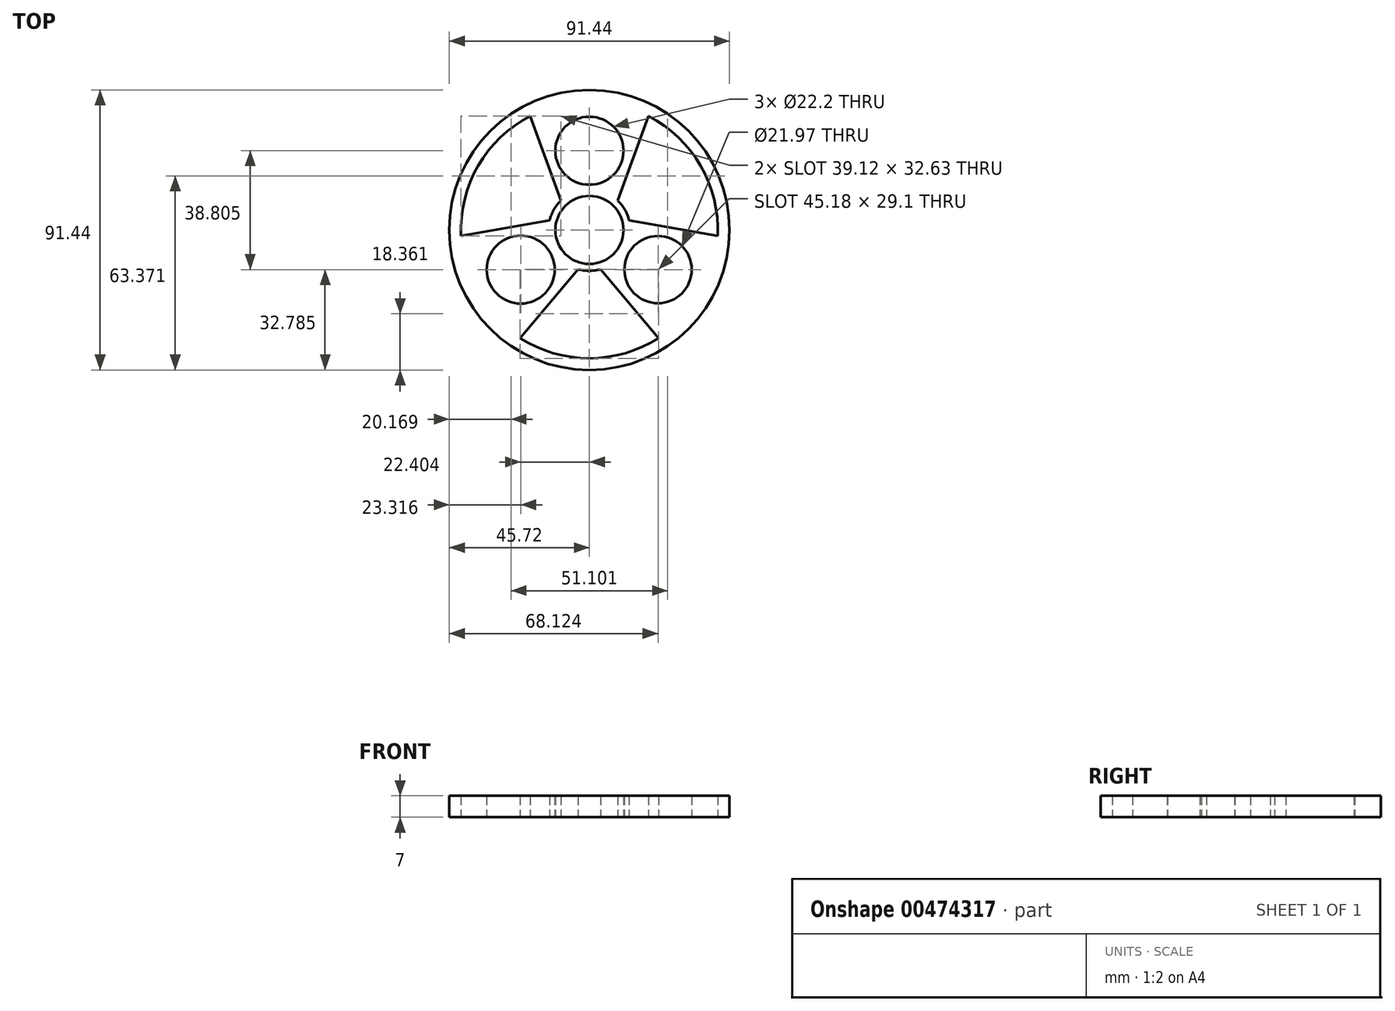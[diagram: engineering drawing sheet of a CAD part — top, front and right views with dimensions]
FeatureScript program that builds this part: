
annotation { "Feature Type Name" : "Feature", "Feature Type Description" : "" }
export const myFeature = defineFeature(function(context is Context, id is Id, definition is map)
    precondition{}
    {
        {
            var Q0;
            Q0=qCreatedBy(makeId("Top.planeOp"),FACE);
            var sketch = newSketch(context, id + "F0", { "sketchPlane" : qUnion([Q0])});
            skCircle(sketch, "E0", {"center": v(0, 0) * mm, "radius": 11.1 * mm});
            skCircle(sketch, "E1", {"center": v(0, 25.87) * mm, "radius": 11.1 * mm});
            skCircle(sketch, "E2.1.1", {"center": v(-22.4, -12.93) * mm, "radius": 11.1 * mm});
            skCircle(sketch, "E2.2.1", {"center": v(22.4, -12.94) * mm, "radius": 10.98 * mm});
            skPoint(sketch, "E3.trimOffspring.end.orphan", {"position": v(15.24, 0) * mm});
            skPoint(sketch, "E4.orphan", {"position": v(-7.62, 13.2) * mm});
            skPoint(sketch, "E5.orphan", {"position": v(-15.24, 0) * mm});
            skPoint(sketch, "E6.orphan", {"position": v(15.24, 40.64) * mm});
            skPoint(sketch, "E7.top.end.orphan", {"position": v(0, 40.64) * mm});
            skPoint(sketch, "E7.top.start.orphan", {"position": v(-15.24, 40.64) * mm});
            skLineSegment(sketch, "E8", {"start": v(8.38, 7.28) * mm, "end": v(19.68, 38.3) * mm});
            skLineSegment(sketch, "E9", {"start": v(-9.23, 9.62) * mm, "end": v(-19.68, 38.3) * mm});
            skArc(sketch, "E10", {"start": v(19.68, 38.3) * mm, "mid": v(0, 43.59) * mm, "end": v(-19.68, 38.3) * mm});
            skLineSegment(sketch, "E11.1.0", {"start": v(-12.95, 3.19) * mm, "end": v(-43.01, -2.11) * mm});
            skLineSegment(sketch, "E11.1.1", {"start": v(-3.71, -12.8) * mm, "end": v(-23.34, -36.2) * mm});
            skArc(sketch, "E11.1.2", {"start": v(-43.01, -2.11) * mm, "mid": v(-37.75, -21.8) * mm, "end": v(-23.34, -36.2) * mm});
            skLineSegment(sketch, "E11.2.0", {"start": v(3.71, -12.8) * mm, "end": v(23.34, -36.2) * mm});
            skLineSegment(sketch, "E11.2.1", {"start": v(12.95, 3.19) * mm, "end": v(43.01, -2.11) * mm});
            skArc(sketch, "E11.2.2", {"start": v(23.34, -36.2) * mm, "mid": v(37.75, -21.8) * mm, "end": v(43.01, -2.11) * mm});
            skArc(sketch, "E12", {"start": v(-3.71, -12.8) * mm, "mid": v(0, -13.34) * mm, "end": v(3.71, -12.8) * mm});
            skPoint(sketch, "E13.orphan", {"position": v(-2.11, -10.9) * mm});
            skPoint(sketch, "E14.orphan", {"position": v(2.11, -10.9) * mm});
            skPoint(sketch, "E15.orphan", {"position": v(10.5, 3.62) * mm});
            skPoint(sketch, "E16.orphan", {"position": v(-8.38, 7.28) * mm});
            skPoint(sketch, "E17.orphan", {"position": v(-10.5, 3.62) * mm});
            skArc(sketch, "E18.trimOffspring", {"start": v(12.95, 3.19) * mm, "mid": v(11.55, 6.67) * mm, "end": v(9.23, 9.62) * mm});
            skArc(sketch, "E19.trimOffspring", {"start": v(-9.23, 9.62) * mm, "mid": v(-11.55, 6.67) * mm, "end": v(-12.95, 3.19) * mm});
            skPoint(sketch, "E20.start.orphan", {"position": v(0, 11.1) * mm});
            skSolve(sketch);
        }
        {
            var Q0;
            Q0 = qSketchRegion(id + "F0", true);
            extrude(context, id + "F1", {"entities" : qUnion([Q0]), "depth" : 7 * mm});
        }
        {
            var Q0;
            Q0=qCreatedBy(makeId("Top.planeOp"),FACE);
            var sketch = newSketch(context, id + "F2", { "sketchPlane" : qUnion([Q0])});
            skCircle(sketch, "E21", {"center": v(0, 0) * mm, "radius": 41.91 * mm});
            skCircle(sketch, "E22", {"center": v(0, 0) * mm, "radius": 45.72 * mm});
            skSolve(sketch);
        }
        {
            var Q0;
            Q0 = qSketchRegion(id + "F2", true);
            extrude(context, id + "F3", {"entities" : qUnion([Q0]), "operationType" : NewBodyOperationType.ADD, "depth" : 7 * mm});
        }
    });
